# Revit family: ПКВ-50А
name_source: partatom
category: Арматура трубопроводов
units: mm (PartAtom-declared; Revit-internal decimal feet)

## family parameters
Всегда вертикально = Да
На основе рабочей плоскости = Нет
Общий = Нет
При загрузке вырезать с полостями = Нет
Размер круглого соединителя = Использовать диаметр
Тип детали = Клапан - Вставляется

## types (6) — shared parameters
ADSK_Единица измерения = шт.
ADSK_Завод-изготовитель = РУП "БЕЛГАЗТЕХНИКА"
ADSK_Количество = 1
ADSK_Максимальное входное давление, МПа = 1,2
ADSK_Марка = ПКВ-50А
ADSK_Масса_Текст = 24,7 кг
ADSK_Пределы настройки автоматического перекрытия подачи газа при повышении контролируемого давления, МПа = 0,03-0,75
ADSK_Пределы настройки автоматического перекрытия подачи газа при понижении контролируемого давления, МПа = 0,003-0,03
ADSK_Тип соединения = фланцевое
ADSK_Тип управляющего сигнала = пневматический
zero-valued in all types: Отметка по умолчанию

## per-type parameters (varying)
| type | ADSK_Диапазон контролируемого давления, МПа | ADSK_Наименование | исполнение 02, 04 | исполнение 03, 05 |
| исполнение 03 0,024-0,1 | 0,024-0,1 | Клапан ПКВ-50А-03  ТУ РБ 00555028-012-94 0,024-0,1 | Нет | Да |
| исполнение 02 0,1-0,3 | 0,1-0,3 | Клапан ПКВ-50А-02  ТУ РБ 00555028-012-94 0,1-0,3 | Да | Нет |
| исполнение 02 0,024-0,1 | 0,024-0,1 | Клапан ПКВ-50А-02  ТУ РБ 00555028-012-94 0,024-0,1 | Да | Нет |
| исполнение 03 0,1-0,3 | 0,1-0,3 | Клапан ПКВ-50А-03  ТУ РБ 00555028-012-94 0,1-0,3 | Нет | Да |
| исполнение 04 0,3-0,6 | 0,3-0,6 | Клапан ПКВ-50А-04  ТУ РБ 00555028-012-94 0,3-0,6 | Да | Нет |
| исполнение 05 0,3-0,6 | 0,3-0,6 | Клапан ПКВ-50А-05  ТУ РБ 00555028-012-94 0,3-0,6 | Нет | Да |
